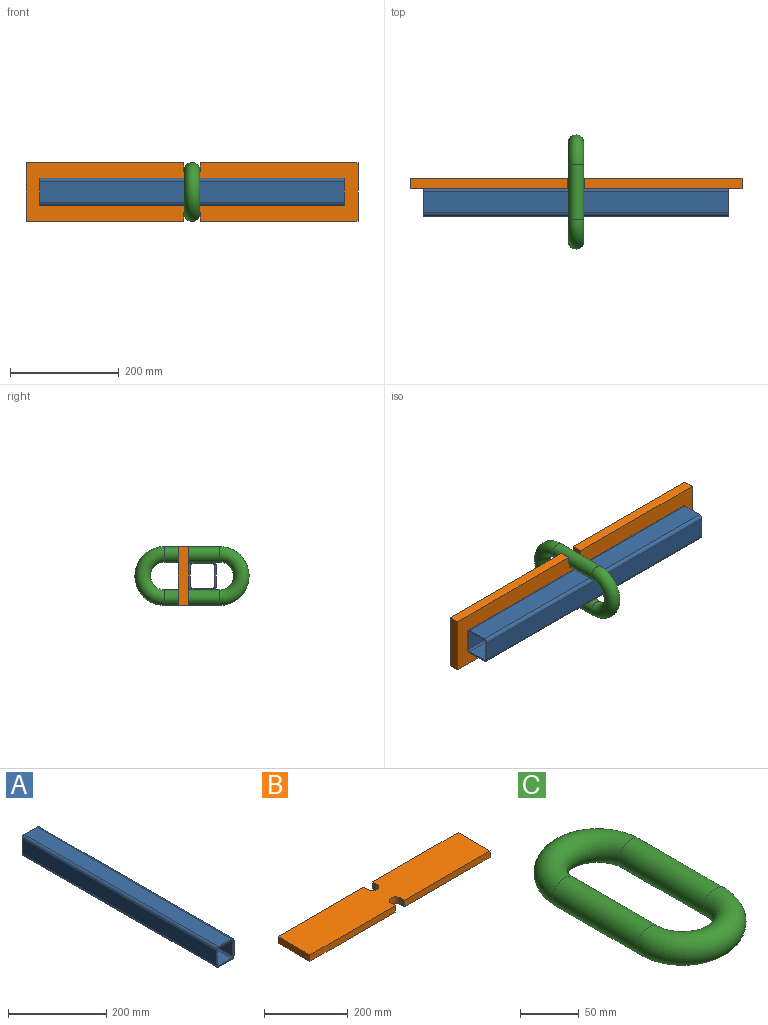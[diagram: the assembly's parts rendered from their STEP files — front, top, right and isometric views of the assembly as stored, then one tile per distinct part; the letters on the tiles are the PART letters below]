
ASSEMBLY  parts=3 mates=2
PART A: 18 faces, bbox 50.8x558.8x50.8 mm
  f0: plane 558.8x38.1mm, normal (0,0,1), area 21290.3mm2, adj f1,f7,f8,f9
  f1: cylinder r=6.35mm len=558.8mm, axis (0,-1,0), area 5573.9mm2, adj f0,f2,f8,f9
  f2: plane 558.8x38.1mm, normal (-1,0,0), area 21290.3mm2, adj f1,f3,f8,f9
  f3: cylinder r=6.35mm len=558.8mm, axis (0,-1,0), area 5573.9mm2, adj f2,f4,f8,f9
  f4: plane 558.8x38.1mm, normal (0,0,-1), area 21290.3mm2, adj f3,f5,f8,f9
  f5: cylinder r=6.35mm len=558.8mm, axis (0,-1,0), area 5573.9mm2, adj f4,f6,f8,f9
  f6: plane 558.8x38.1mm, normal (1,0,0), area 21290.3mm2, adj f5,f7,f8,f9
  f7: cylinder r=6.35mm len=558.8mm, axis (0,-1,0), area 5573.9mm2, adj f0,f6,f8,f9
  f8: plane 50.8x50.8mm, normal (0,1,0), area 578.9mm2, adj f0,f1,f2,f3,f4,f5,f6,f7
  f9: plane 50.8x50.8mm, normal (0,-1,0), area 578.9mm2, adj f0,f1,f2,f3,f4,f5,f6,f7
  f10: cylinder r=3.17mm len=558.8mm, axis (0,-1,0), area 2786.9mm2, adj f8,f9,f11,f17
  f11: plane 558.8x38.1mm, normal (1,0,0), area 21290.3mm2, adj f8,f9,f10,f12
  f12: cylinder r=3.17mm len=558.8mm, axis (0,-1,0), area 2786.9mm2, adj f8,f9,f11,f13
  f13: plane 558.8x38.1mm, normal (0,0,-1), area 21290.3mm2, adj f8,f9,f12,f14
  f14: cylinder r=3.17mm len=558.8mm, axis (0,-1,0), area 2786.9mm2, adj f8,f9,f13,f15
  f15: plane 558.8x38.1mm, normal (-1,0,0), area 21290.3mm2, adj f8,f9,f14,f16
  f16: cylinder r=3.17mm len=558.8mm, axis (0,-1,0), area 2786.9mm2, adj f8,f9,f15,f17
  f17: plane 558.8x38.1mm, normal (0,0,1), area 21290.3mm2, adj f8,f9,f10,f16
PART B: 14 faces, bbox 609.6x108x19.1 mm
  f0: cylinder r=15.08mm len=30.16mm, axis (0,0,-1), area 902.6mm2, adj f1,f11,f12,f13
  f1: plane 19.05x14.29mm, normal (1,0,0), area 272.2mm2, adj f0,f2,f12,f13
  f2: plane 289.72x19.05mm, normal (0,1,0), area 5519.1mm2, adj f1,f3,f12,f13
  f3: plane 107.95x19.05mm, normal (-1,0,0), area 2056.4mm2, adj f2,f4,f12,f13
  f4: plane 289.72x19.05mm, normal (0,-1,0), area 5519.1mm2, adj f3,f5,f12,f13
  f5: plane 19.05x14.29mm, normal (1,0,0), area 272.2mm2, adj f4,f6,f12,f13
  f6: cylinder r=15.08mm len=30.16mm, axis (0,0,-1), area 902.6mm2, adj f5,f7,f12,f13
  f7: plane 19.05x14.29mm, normal (-1,0,0), area 272.2mm2, adj f6,f8,f12,f13
  f8: plane 289.72x19.05mm, normal (0,-1,0), area 5519.1mm2, adj f7,f9,f12,f13
  f9: plane 107.95x19.05mm, normal (1,0,0), area 2056.4mm2, adj f8,f10,f12,f13
  f10: plane 289.72x19.05mm, normal (0,1,0), area 5519.1mm2, adj f9,f11,f12,f13
  f11: plane 19.05x14.29mm, normal (-1,0,0), area 272.2mm2, adj f0,f10,f12,f13
  f12: plane 609.6x107.95mm, normal (0,0,1), area 64229.9mm2, adj f0,f1,f2,f3,f4,f5,f6,f7
  f13: plane 609.6x107.95mm, normal (0,0,-1), area 64229.9mm2, adj f0,f1,f2,f3,f4,f5,f6,f7
PART C: 4 faces, bbox 116.8x218.4x28.6 mm
  f0: torus R=39.69mm, axis (0,0,-1), area 11192.8mm2, adj f1,f3
  f1: cylinder r=14.29mm len=101.6mm, axis (0,1,0), area 9120.7mm2, adj f0,f2
  f2: torus R=39.69mm, axis (0,0,-1), area 11192.8mm2, adj f1,f3
  f3: cylinder r=14.29mm len=101.6mm, axis (0,-1,0), area 9120.7mm2, adj f0,f2
PLACE A rot(axis=(0,0,-1),90deg) t=(370.5,32.49,98.65)mm
PLACE B rot(axis=(1,0,0),90deg) t=(91.1,76.94,98.65)mm
PLACE C rot(axis=(0,1,0),90deg) t=(91.1,51.54,98.65)mm
MATE fastened B.f0 <-> C.f1  axis (0,1,0) through (91.1,76.94,138.34)mm
MATE fastened A.f2 <-> B.f12  axis (0,1,0) through (91.1,57.89,98.65)mm
